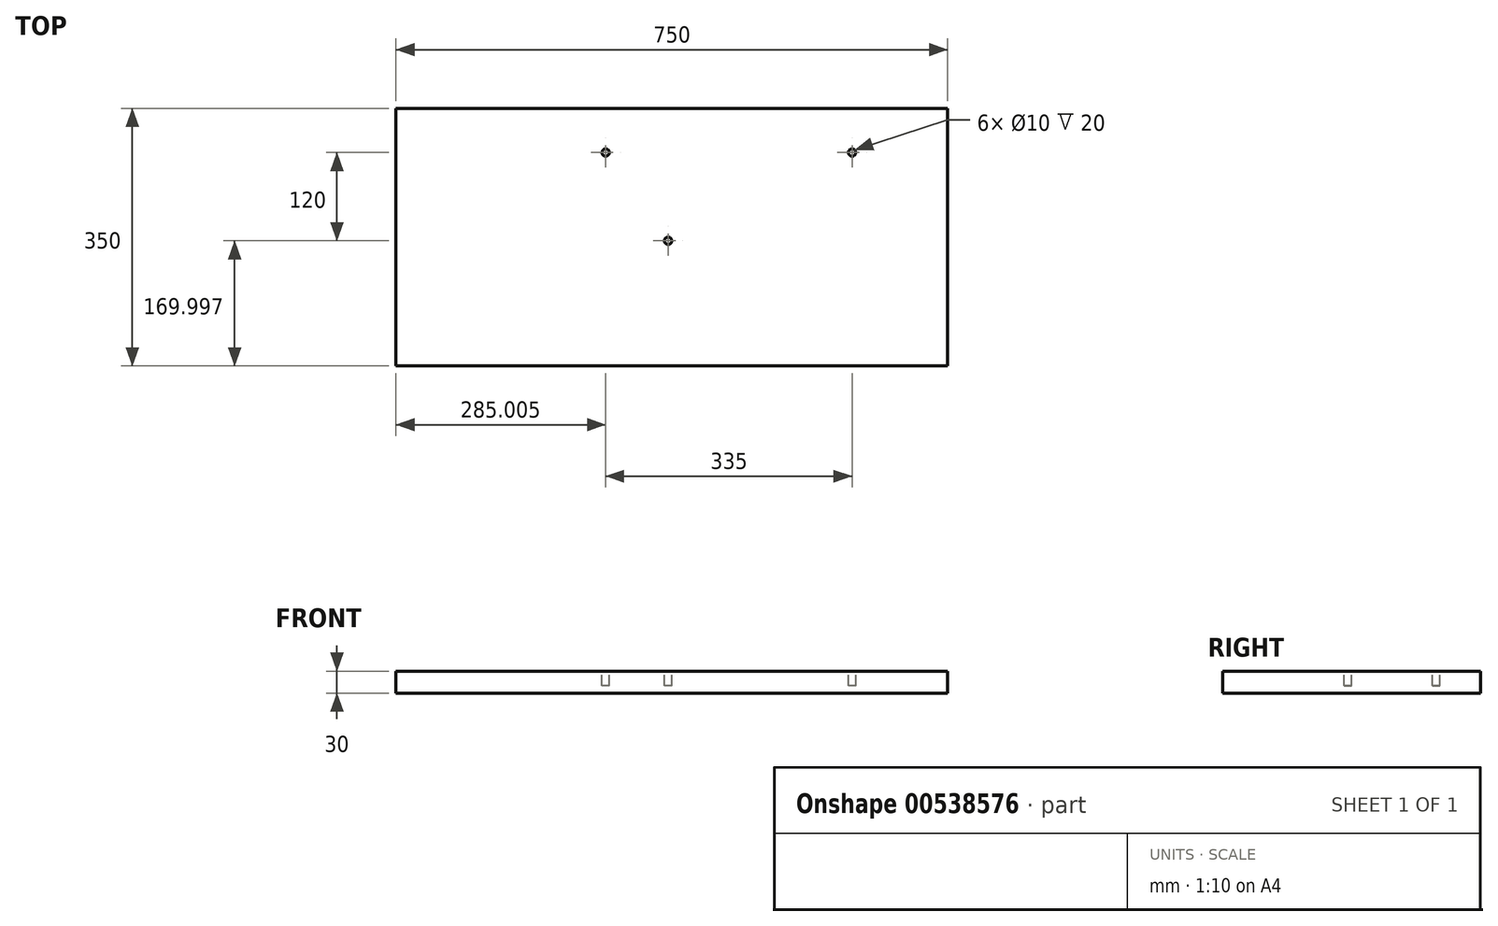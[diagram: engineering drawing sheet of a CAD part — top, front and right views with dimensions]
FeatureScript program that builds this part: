
annotation { "Feature Type Name" : "Feature", "Feature Type Description" : "" }
export const myFeature = defineFeature(function(context is Context, id is Id, definition is map)
    precondition{}
    {
        {
            var Q0;
            Q0=qCreatedBy(makeId("Top.planeOp"),FACE);
            var sketch = newSketch(context, id + "F0", { "sketchPlane" : qUnion([Q0])});
            skLineSegment(sketch, "E0.bottom", {"start": v(-735.5, 333.74) * mm, "end": v(14.5, 333.74) * mm});
            skLineSegment(sketch, "E0.top", {"start": v(-735.5, -16.26) * mm, "end": v(14.5, -16.26) * mm});
            skLineSegment(sketch, "E0.left", {"start": v(-735.5, 333.74) * mm, "end": v(-735.5, -16.26) * mm});
            skLineSegment(sketch, "E0.right", {"start": v(14.5, 333.74) * mm, "end": v(14.5, -16.26) * mm});
            skSolve(sketch);
        }
        {
            var Q0;
            Q0 = qSketchRegion(id + "F0", true);
            extrude(context, id + "F1", {"entities" : qUnion([Q0]), "depth" : 30 * mm, "offsetDistance" : 25 * mm});
        }
        {
            var Q0;
            Q0=makeQuery(id+"F1.opExtrude","CAP_FACE",FACE,{"disambiguationData":[OSD([sQuery(id+"F0.wireOp",EDGE,"E0.bottom"),sQuery(id+"F0.wireOp",EDGE,"E0.top"),sQuery(id+"F0.wireOp",EDGE,"E0.left"),sQuery(id+"F0.wireOp",EDGE,"E0.right")])],"isStart":false});
            var sketch = newSketch(context, id + "F2", { "sketchPlane" : qUnion([Q0])});
            skCircle(sketch, "E1", {"center": v(-365.5, 153.74) * mm, "radius": 5 * mm});
            skSolve(sketch);
        }
        {
            var Q0;
            Q0=makeQuery(id+"F2.imprint","IMPRINT",FACE,{"disambiguationData":[TD([[makeQuery(id+"F2.imprint","IMPRINT",EDGE,{"derivedFrom":sQuery(id+"F2.wireOp",EDGE,"E1")}),1.0]])]});
            extrude(context, id + "F3", {"entities" : qUnion([Q0]), "operationType" : NewBodyOperationType.REMOVE, "oppositeDirection" : true, "depth" : 20 * mm, "offsetDistance" : 25 * mm});
        }
        {
            var Q0;
            Q0=makeQuery(id+"F1.opExtrude","CAP_FACE",FACE,{"disambiguationData":[OSD([sQuery(id+"F0.wireOp",EDGE,"E0.bottom"),sQuery(id+"F0.wireOp",EDGE,"E0.top"),sQuery(id+"F0.wireOp",EDGE,"E0.left"),sQuery(id+"F0.wireOp",EDGE,"E0.right")])],"isStart":false});
            var sketch = newSketch(context, id + "F4", { "sketchPlane" : qUnion([Q0])});
            skCircle(sketch, "E2", {"center": v(-450.5, 273.74) * mm, "radius": 5 * mm});
            skSolve(sketch);
        }
        {
            var Q0;
            Q0=makeQuery(id+"F4.imprint","IMPRINT",FACE,{"disambiguationData":[TD([[makeQuery(id+"F4.imprint","IMPRINT",EDGE,{"derivedFrom":sQuery(id+"F4.wireOp",EDGE,"E2")}),1.0]])]});
            extrude(context, id + "F5", {"entities" : qUnion([Q0]), "operationType" : NewBodyOperationType.REMOVE, "oppositeDirection" : true, "depth" : 20 * mm, "offsetDistance" : 25 * mm});
        }
        {
            var Q0;
            Q0=makeQuery(id+"F1.opExtrude","CAP_FACE",FACE,{"disambiguationData":[OSD([sQuery(id+"F0.wireOp",EDGE,"E0.bottom"),sQuery(id+"F0.wireOp",EDGE,"E0.top"),sQuery(id+"F0.wireOp",EDGE,"E0.left"),sQuery(id+"F0.wireOp",EDGE,"E0.right")])],"isStart":false});
            var sketch = newSketch(context, id + "F6", { "sketchPlane" : qUnion([Q0])});
            skCircle(sketch, "E3", {"center": v(-115.5, 273.74) * mm, "radius": 5 * mm});
            skSolve(sketch);
        }
        {
            var Q0;
            Q0=makeQuery(id+"F6.imprint","IMPRINT",FACE,{"disambiguationData":[TD([[makeQuery(id+"F6.imprint","IMPRINT",EDGE,{"derivedFrom":sQuery(id+"F6.wireOp",EDGE,"E3")}),1.0]])]});
            extrude(context, id + "F7", {"entities" : qUnion([Q0]), "operationType" : NewBodyOperationType.REMOVE, "oppositeDirection" : true, "depth" : 20 * mm, "offsetDistance" : 25 * mm});
        }
    });
